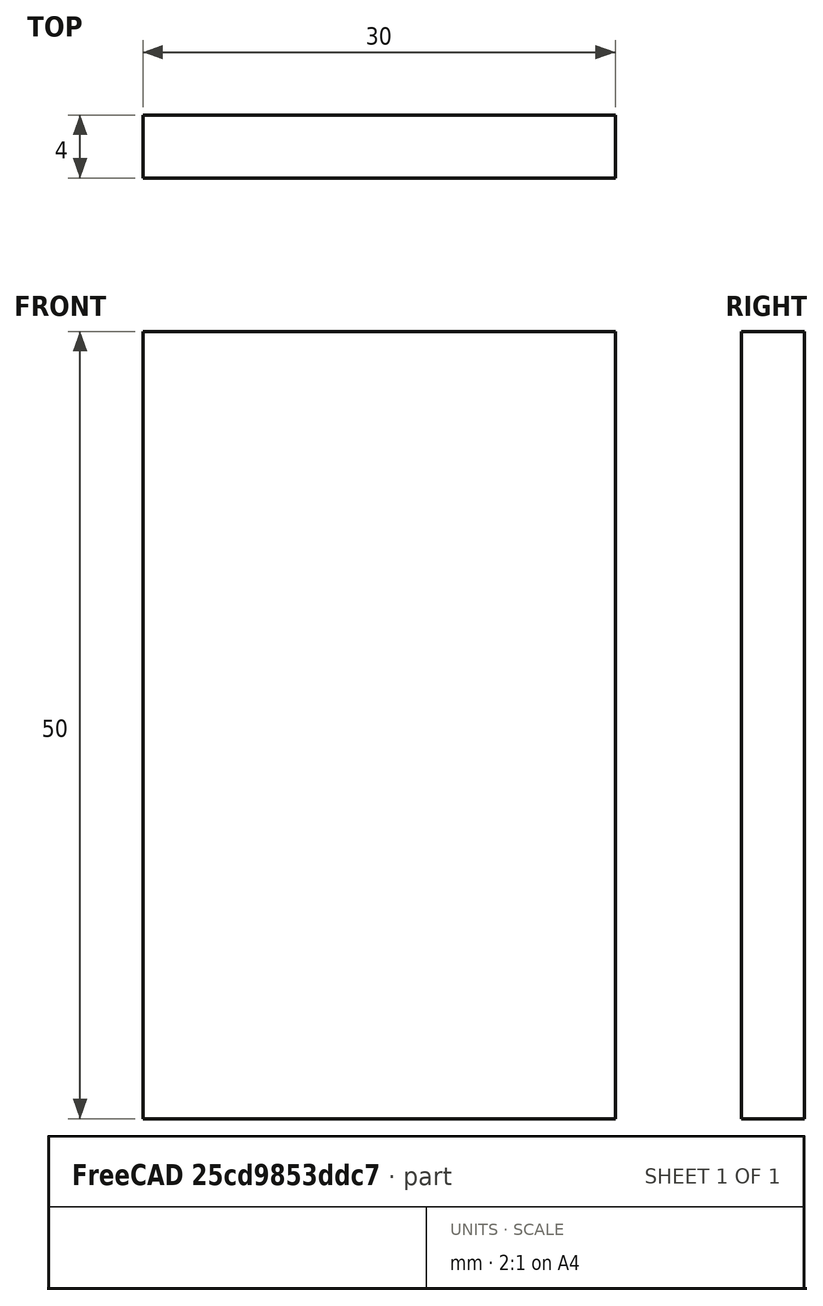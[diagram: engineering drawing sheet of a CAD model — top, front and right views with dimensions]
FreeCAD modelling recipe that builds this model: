
FCSTD DOCUMENT  (FreeCAD 0.15R4671 (Git))
Label: Flat Bar 30x4 EN10058 S235JR
License: All rights reserved
LicenseURL: http://en.wikipedia.org/wiki/All_rights_reserved
objects: Sketcher::SketchObject×1, Part::Extrusion×1
note: 2 computed .brp shape members not serialized (recipe doc carries the construction recipe); baked Part::Feature solids carry a one-line shape summary decoded from their .brp

FEATURE [Sketcher::SketchObject] Sketch
  sketch-geometry (4):
    g0: LineSegment StartX=-15 StartY=-2 StartZ=0 EndX=15 EndY=-2 EndZ=0
    g1: LineSegment StartX=15 StartY=-2 StartZ=0 EndX=15 EndY=2 EndZ=0
    g2: LineSegment StartX=15 StartY=2 StartZ=0 EndX=-15 EndY=2 EndZ=0
    g3: LineSegment StartX=-15 StartY=2 StartZ=0 EndX=-15 EndY=-2 EndZ=0
  constraints (12):
    c: Coincident(g0,g1)
    c: Coincident(g1,g2)
    c: Coincident(g2,g3)
    c: Coincident(g3,g0)
    c: Horizontal(g0)
    c: Horizontal(g2)
    c: Vertical(g1)
    c: Vertical(g3)
    c: Symmetric(g1,g2,g-2)
    c: Symmetric(g0,g1,g-1)
    c: DistanceY(g1) = 4
    c: DistanceX(g0) = 30
FEATURE [Part::Extrusion] Extrude  label="Flat Bar 30x4 EN10058 S235JR"
  Base = -> Sketch
  Dir = (0,0,50)
  Solid = true
